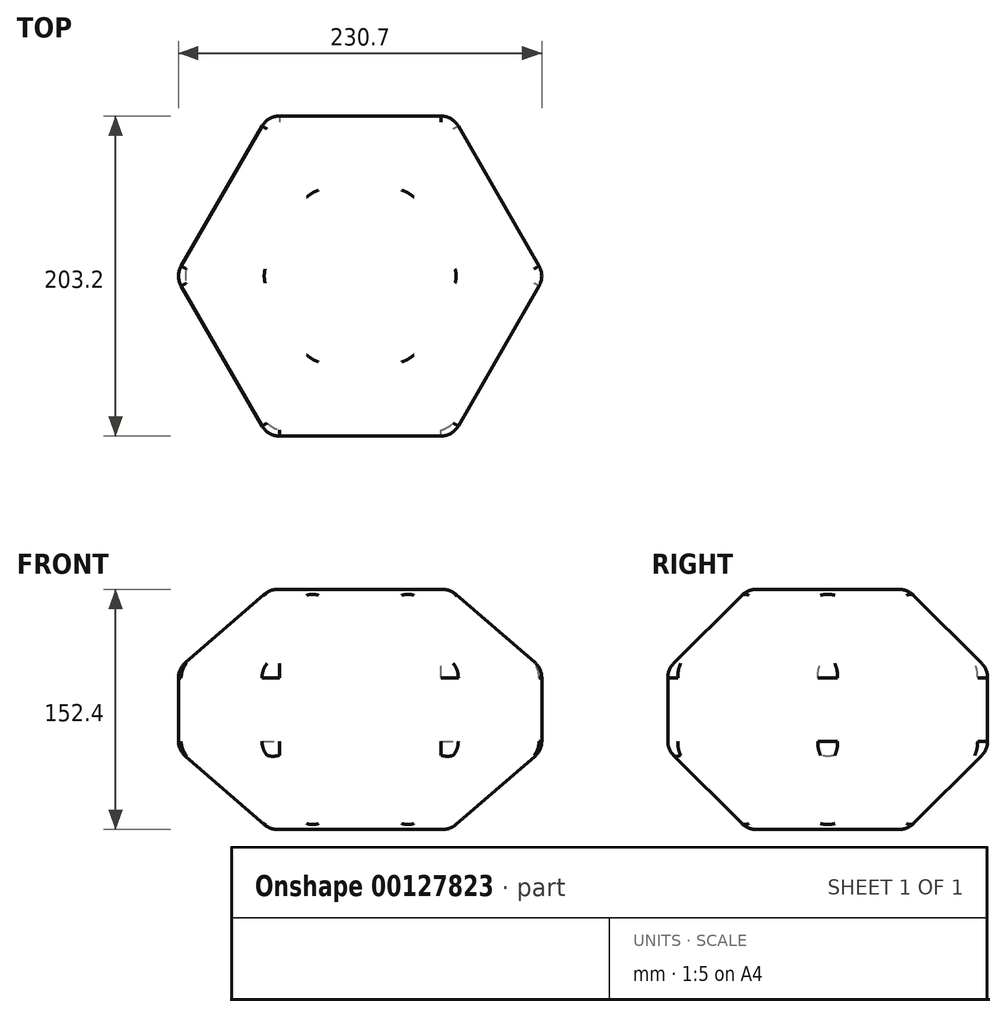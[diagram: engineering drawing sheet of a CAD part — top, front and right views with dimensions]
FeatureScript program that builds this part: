
annotation { "Feature Type Name" : "Feature", "Feature Type Description" : "" }
export const myFeature = defineFeature(function(context is Context, id is Id, definition is map)
    precondition{}
    {
        {
            var Q0;
            Q0=qCreatedBy(makeId("Top.planeOp"),FACE);
            var sketch = newSketch(context, id + "F0", { "sketchPlane" : qUnion([Q0])});
            skCircle(sketch, "E0.cCircle", {"center": v(0, 0) * mm, "radius": 101.6 * mm, "construction": true});
            skLineSegment(sketch, "E0.0", {"start": v(-58.66, 101.6) * mm, "end": v(58.66, 101.6) * mm});
            skLineSegment(sketch, "E0.1", {"start": v(58.66, 101.6) * mm, "end": v(117.32, 0) * mm});
            skLineSegment(sketch, "E0.2", {"start": v(117.32, 0) * mm, "end": v(58.66, -101.6) * mm});
            skLineSegment(sketch, "E0.3", {"start": v(58.66, -101.6) * mm, "end": v(-58.66, -101.6) * mm});
            skLineSegment(sketch, "E0.4", {"start": v(-58.66, -101.6) * mm, "end": v(-117.32, 0) * mm});
            skLineSegment(sketch, "E0.5", {"start": v(-117.32, 0) * mm, "end": v(-58.66, 101.6) * mm});
            skPoint(sketch, "E0.0.midPoint", {"position": v(0, 101.6) * mm});
            skSolve(sketch);
        }
        {
            var Q0;
            Q0=makeQuery(id+"F0.imprint","IMPRINT",FACE,{"disambiguationData":[TD([[makeQuery(id+"F0.imprint","IMPRINT",EDGE,{"derivedFrom":sQuery(id+"F0.wireOp",EDGE,"E0.0")}),-1.0]])]});
            extrude(context, id + "F1", {"entities" : qUnion([Q0]), "depth" : 152.4 * mm});
        }
        {
            var Q0;
            Q0=makeQuery(id+"F1.opExtrude","CAP_EDGE",EDGE,{"disambiguationData":[OSD([sQuery(id+"F0.wireOp",EDGE,"E0.4")])],"isStart":false});
            var Q1;
            Q1=makeQuery(id+"F1.opExtrude","CAP_EDGE",EDGE,{"disambiguationData":[OSD([sQuery(id+"F0.wireOp",EDGE,"E0.3")])],"isStart":false});
            var Q2;
            Q2=makeQuery(id+"F1.opExtrude","CAP_EDGE",EDGE,{"disambiguationData":[OSD([sQuery(id+"F0.wireOp",EDGE,"E0.2")])],"isStart":false});
            var Q3;
            Q3=makeQuery(id+"F1.opExtrude","CAP_EDGE",EDGE,{"disambiguationData":[OSD([sQuery(id+"F0.wireOp",EDGE,"E0.1")])],"isStart":false});
            var Q4;
            Q4=makeQuery(id+"F1.opExtrude","CAP_EDGE",EDGE,{"disambiguationData":[OSD([sQuery(id+"F0.wireOp",EDGE,"E0.0")])],"isStart":false});
            var Q5;
            Q5=makeQuery(id+"F1.opExtrude","CAP_EDGE",EDGE,{"disambiguationData":[OSD([sQuery(id+"F0.wireOp",EDGE,"E0.5")])],"isStart":false});
            chamfer(context, id + "F2", {"entities" : qUnion([Q0, Q1, Q2, Q3, Q4, Q5]), "width" : 50.8 * mm, "tangentPropagation" : true});
        }
        {
            var Q0;
            Q0=makeQuery(id+"F1.opExtrude","CAP_EDGE",EDGE,{"disambiguationData":[OSD([sQuery(id+"F0.wireOp",EDGE,"E0.4")])],"isStart":true});
            var Q1;
            Q1=makeQuery(id+"F1.opExtrude","CAP_EDGE",EDGE,{"disambiguationData":[OSD([sQuery(id+"F0.wireOp",EDGE,"E0.3")])],"isStart":true});
            var Q2;
            Q2=makeQuery(id+"F1.opExtrude","CAP_EDGE",EDGE,{"disambiguationData":[OSD([sQuery(id+"F0.wireOp",EDGE,"E0.2")])],"isStart":true});
            var Q3;
            Q3=makeQuery(id+"F1.opExtrude","CAP_EDGE",EDGE,{"disambiguationData":[OSD([sQuery(id+"F0.wireOp",EDGE,"E0.1")])],"isStart":true});
            var Q4;
            Q4=makeQuery(id+"F1.opExtrude","CAP_EDGE",EDGE,{"disambiguationData":[OSD([sQuery(id+"F0.wireOp",EDGE,"E0.0")])],"isStart":true});
            var Q5;
            Q5=makeQuery(id+"F1.opExtrude","CAP_EDGE",EDGE,{"disambiguationData":[OSD([sQuery(id+"F0.wireOp",EDGE,"E0.5")])],"isStart":true});
            chamfer(context, id + "F3", {"entities" : qUnion([Q0, Q1, Q2, Q3, Q4, Q5]), "width" : 50.8 * mm, "tangentPropagation" : true});
        }
        {
            var Q0;
            Q0=makeQuery(id+"F1.opExtrude","CAP_FACE",FACE,{"disambiguationData":[OSD([sQuery(id+"F0.wireOp",EDGE,"E0.0"),sQuery(id+"F0.wireOp",EDGE,"E0.1"),sQuery(id+"F0.wireOp",EDGE,"E0.2"),sQuery(id+"F0.wireOp",EDGE,"E0.3"),sQuery(id+"F0.wireOp",EDGE,"E0.4"),sQuery(id+"F0.wireOp",EDGE,"E0.5")])],"isStart":false});
            var Q1;
            Q1=makeQuery(id+"F2.opChamfer","BLEND_FACE",FACE,{"disambiguationData":[OSD([sQuery(id+"F0.wireOp",EDGE,"E0.4")])]});
            var Q2;
            Q2=makeQuery(id+"F2.opChamfer","BLEND_FACE",FACE,{"disambiguationData":[OSD([sQuery(id+"F0.wireOp",EDGE,"E0.3")])]});
            var Q3;
            Q3=makeQuery(id+"F2.opChamfer","BLEND_FACE",FACE,{"disambiguationData":[OSD([sQuery(id+"F0.wireOp",EDGE,"E0.2")])]});
            var Q4;
            Q4=makeQuery(id+"F1.opExtrude","SWEPT_FACE",FACE,{"disambiguationData":[OSD([sQuery(id+"F0.wireOp",EDGE,"E0.3")])]});
            var Q5;
            Q5=makeQuery(id+"F3.opChamfer","BLEND_FACE",FACE,{"disambiguationData":[OSD([sQuery(id+"F0.wireOp",EDGE,"E0.3")])]});
            var Q6;
            Q6=makeQuery(id+"F1.opExtrude","SWEPT_FACE",FACE,{"disambiguationData":[OSD([sQuery(id+"F0.wireOp",EDGE,"E0.4")])]});
            var Q7;
            Q7=makeQuery(id+"F3.opChamfer","BLEND_FACE",FACE,{"disambiguationData":[OSD([sQuery(id+"F0.wireOp",EDGE,"E0.4")])]});
            var Q8;
            Q8=makeQuery(id+"F2.opChamfer","BLEND_FACE",FACE,{"disambiguationData":[OSD([sQuery(id+"F0.wireOp",EDGE,"E0.5")])]});
            var Q9;
            Q9=makeQuery(id+"F1.opExtrude","SWEPT_FACE",FACE,{"disambiguationData":[OSD([sQuery(id+"F0.wireOp",EDGE,"E0.5")])]});
            var Q10;
            Q10=makeQuery(id+"F3.opChamfer","BLEND_FACE",FACE,{"disambiguationData":[OSD([sQuery(id+"F0.wireOp",EDGE,"E0.5")])]});
            var Q11;
            Q11=makeQuery(id+"F2.opChamfer","BLEND_FACE",FACE,{"disambiguationData":[OSD([sQuery(id+"F0.wireOp",EDGE,"E0.0")])]});
            var Q12;
            Q12=makeQuery(id+"F1.opExtrude","SWEPT_FACE",FACE,{"disambiguationData":[OSD([sQuery(id+"F0.wireOp",EDGE,"E0.0")])]});
            var Q13;
            Q13=makeQuery(id+"F3.opChamfer","BLEND_FACE",FACE,{"disambiguationData":[OSD([sQuery(id+"F0.wireOp",EDGE,"E0.0")])]});
            var Q14;
            Q14=makeQuery(id+"F2.opChamfer","BLEND_FACE",FACE,{"disambiguationData":[OSD([sQuery(id+"F0.wireOp",EDGE,"E0.1")])]});
            var Q15;
            Q15=makeQuery(id+"F1.opExtrude","SWEPT_FACE",FACE,{"disambiguationData":[OSD([sQuery(id+"F0.wireOp",EDGE,"E0.1")])]});
            var Q16;
            Q16=makeQuery(id+"F3.opChamfer","BLEND_FACE",FACE,{"disambiguationData":[OSD([sQuery(id+"F0.wireOp",EDGE,"E0.1")])]});
            var Q17;
            Q17=makeQuery(id+"F3.opChamfer","BLEND_FACE",FACE,{"disambiguationData":[OSD([sQuery(id+"F0.wireOp",EDGE,"E0.2")])]});
            var Q18;
            Q18=makeQuery(id+"F1.opExtrude","CAP_FACE",FACE,{"disambiguationData":[OSD([sQuery(id+"F0.wireOp",EDGE,"E0.0"),sQuery(id+"F0.wireOp",EDGE,"E0.1"),sQuery(id+"F0.wireOp",EDGE,"E0.2"),sQuery(id+"F0.wireOp",EDGE,"E0.3"),sQuery(id+"F0.wireOp",EDGE,"E0.4"),sQuery(id+"F0.wireOp",EDGE,"E0.5")])],"isStart":true});
            fillet(context, id + "F4", {"entities" : qUnion([Q0, Q1, Q2, Q3, Q4, Q5, Q6, Q7, Q8, Q9, Q10, Q11, Q12, Q13, Q14, Q15, Q16, Q17, Q18]), "radius" : 12.7 * mm, "tangentPropagation" : true, "allowEdgeOverflow" : false});
        }
    });
